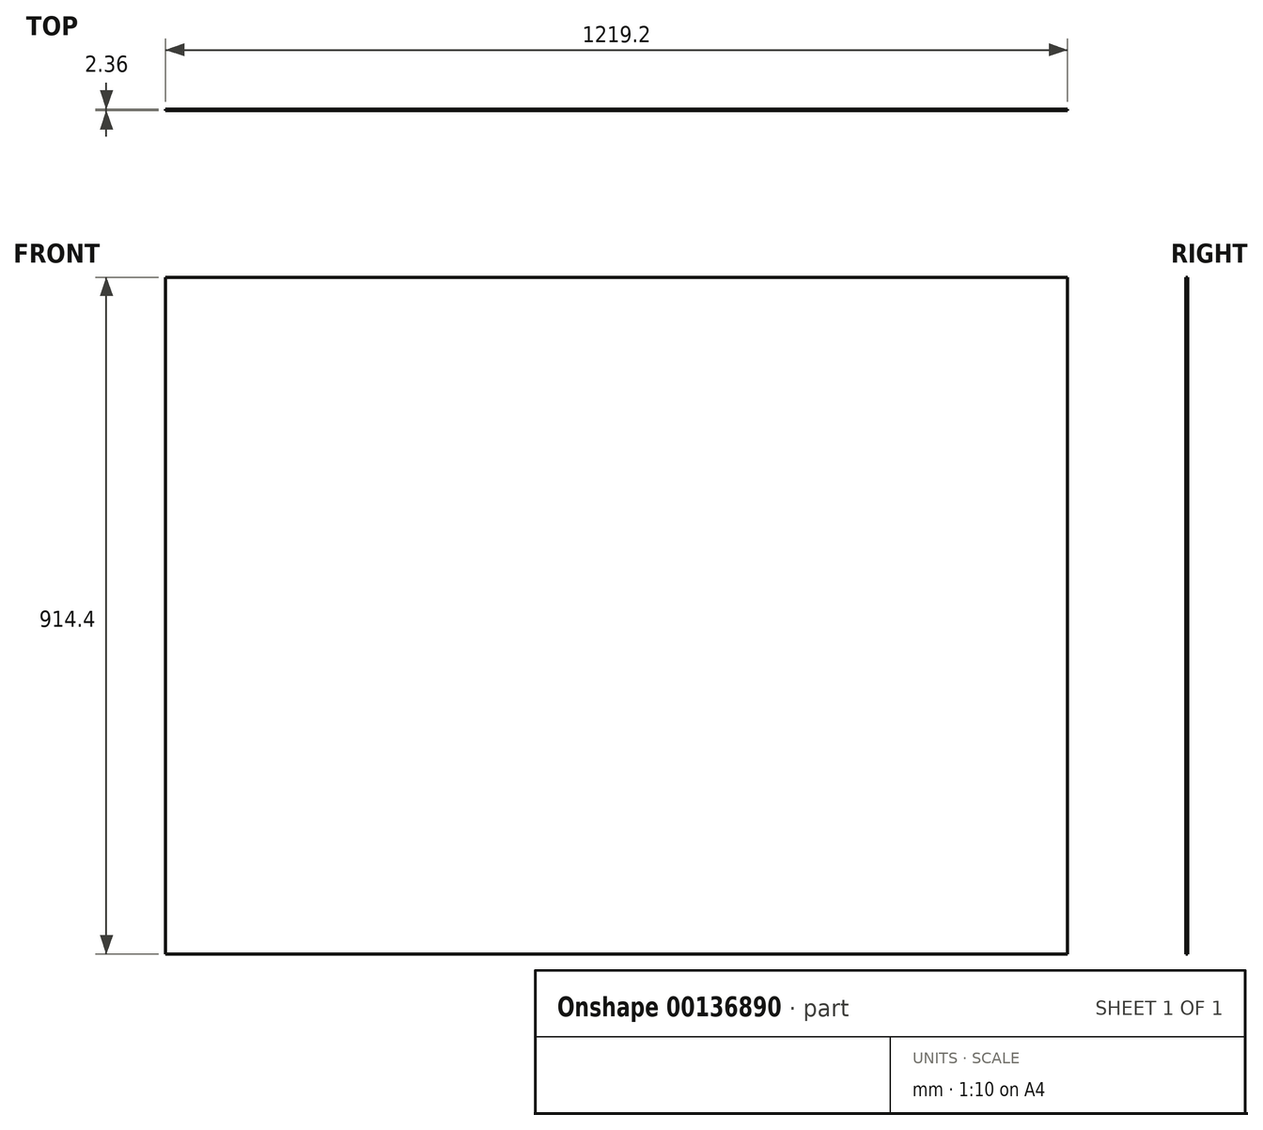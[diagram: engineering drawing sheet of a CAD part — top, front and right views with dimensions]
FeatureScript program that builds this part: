
annotation { "Feature Type Name" : "Feature", "Feature Type Description" : "" }
export const myFeature = defineFeature(function(context is Context, id is Id, definition is map)
    precondition{}
    {
        {
            var Q0;
            Q0=qCreatedBy(makeId("Front.planeOp"),FACE);
            var sketch = newSketch(context, id + "F0", { "sketchPlane" : qUnion([Q0])});
            skLineSegment(sketch, "E0.bottom", {"start": v(0, 0) * mm, "end": v(1219.2, 0) * mm});
            skLineSegment(sketch, "E0.top", {"start": v(0, 914.4) * mm, "end": v(1219.2, 914.4) * mm});
            skLineSegment(sketch, "E0.left", {"start": v(0, 0) * mm, "end": v(0, 914.4) * mm});
            skLineSegment(sketch, "E0.right", {"start": v(1219.2, 0) * mm, "end": v(1219.2, 914.4) * mm});
            skSolve(sketch);
        }
        {
            var Q0;
            Q0=makeQuery(id+"F0.imprint","IMPRINT",FACE,{"disambiguationData":[TD([[makeQuery(id+"F0.imprint","IMPRINT",EDGE,{"derivedFrom":sQuery(id+"F0.wireOp",EDGE,"E0.bottom")}),1.0]])]});
            extrude(context, id + "F1", {"entities" : qUnion([Q0]), "depth" : 2.36 * mm});
        }
    });
